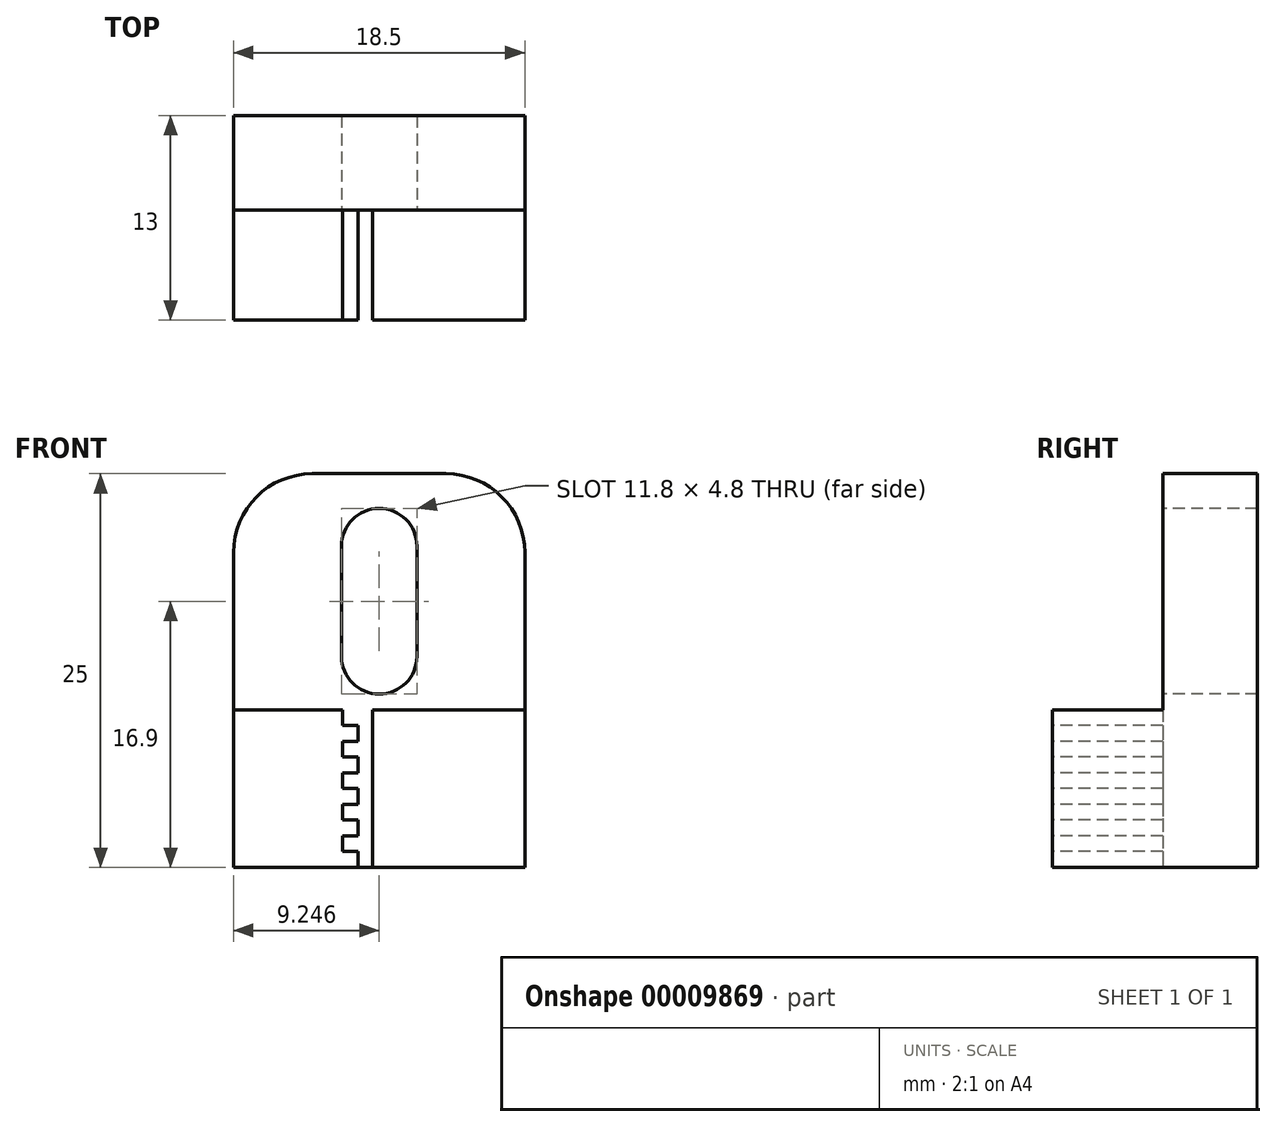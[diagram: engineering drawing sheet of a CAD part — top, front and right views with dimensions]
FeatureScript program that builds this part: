
annotation { "Feature Type Name" : "Feature", "Feature Type Description" : "" }
export const myFeature = defineFeature(function(context is Context, id is Id, definition is map)
    precondition{}
    {
        {
            var Q0;
            Q0=qCreatedBy(makeId("Top.planeOp"),FACE);
            var sketch = newSketch(context, id + "F0", { "sketchPlane" : qUnion([Q0])});
            skLineSegment(sketch, "E0.bottom", {"start": v(-4.96, 0) * mm, "end": v(13.54, 0) * mm});
            skLineSegment(sketch, "E0.top", {"start": v(-4.96, 25) * mm, "end": v(13.54, 25) * mm});
            skLineSegment(sketch, "E0.left", {"start": v(-4.96, 0) * mm, "end": v(-4.96, 25) * mm});
            skLineSegment(sketch, "E0.right", {"start": v(13.54, 0) * mm, "end": v(13.54, 25) * mm});
            skLineSegment(sketch, "E1", {"start": v(-4.96, 5) * mm, "end": v(13.54, 5) * mm});
            skLineSegment(sketch, "E2.bottom", {"start": v(-4.96, 17.95) * mm, "end": v(-1.96, 17.95) * mm});
            skLineSegment(sketch, "E2.top", {"start": v(-4.96, 12.05) * mm, "end": v(-1.96, 12.05) * mm});
            skLineSegment(sketch, "E2.left", {"start": v(-4.96, 17.95) * mm, "end": v(-4.96, 12.05) * mm});
            skLineSegment(sketch, "E2.right", {"start": v(-1.96, 17.95) * mm, "end": v(-1.96, 12.05) * mm});
            skLineSegment(sketch, "E3.bottom", {"start": v(13.54, 17.95) * mm, "end": v(10.54, 17.95) * mm});
            skLineSegment(sketch, "E3.top", {"start": v(13.54, 12.05) * mm, "end": v(10.54, 12.05) * mm});
            skLineSegment(sketch, "E3.left", {"start": v(13.54, 17.95) * mm, "end": v(13.54, 12.05) * mm});
            skLineSegment(sketch, "E3.right", {"start": v(10.54, 17.95) * mm, "end": v(10.54, 12.05) * mm});
            skPoint(sketch, "E4", {"position": v(-1.96, 15) * mm});
            skPoint(sketch, "E5", {"position": v(-4.96, 15) * mm});
            skLineSegment(sketch, "E6", {"start": v(-4.96, 15) * mm, "end": v(13.54, 15) * mm});
            skLineSegment(sketch, "E7", {"start": v(-4.96, 13) * mm, "end": v(13.54, 13) * mm});
            skSolve(sketch);
        }
        {
            var Q0;
            {var subQ0=sQuery(id+"F0.wireOp",EDGE,"E0.bottom");Q0=makeQuery(id+"F0.imprint","IMPRINT",FACE,{"disambiguationData":[TD([[makeQuery(id+"F0.imprint","IMPRINT",EDGE,{"derivedFrom":subQ0}),1.0]])]});}
            var Q1;
            {var subQ0=sQuery(id+"F0.wireOp",EDGE,"E1");Q1=makeQuery(id+"F0.imprint","IMPRINT",FACE,{"disambiguationData":[TD([[makeQuery(id+"F0.imprint","IMPRINT",EDGE,{"derivedFrom":subQ0}),1.0]])]});}
            var Q2;
            {var subQ0=sQuery(id+"F0.wireOp",EDGE,"E2.top");Q2=makeQuery(id+"F0.imprint","IMPRINT",FACE,{"disambiguationData":[TD([[makeQuery(id+"F0.imprint","IMPRINT",EDGE,{"derivedFrom":subQ0}),1.0]])]});}
            var Q3;
            {var subQ0=sQuery(id+"F0.wireOp",EDGE,"E3.top");Q3=makeQuery(id+"F0.imprint","IMPRINT",FACE,{"disambiguationData":[TD([[makeQuery(id+"F0.imprint","IMPRINT",EDGE,{"derivedFrom":subQ0}),-1.0]])]});}
            extrude(context, id + "F1", {"entities" : qUnion([Q0, Q1, Q2, Q3]), "depth" : 10 * mm});
        }
        {
            var Q0;
            Q0=makeQuery(id+"F1.opExtrude","SWEPT_FACE",FACE,{"disambiguationData":[OSD([sQuery(id+"F0.wireOp",EDGE,"E0.bottom")])]});
            var sketch = newSketch(context, id + "F2", { "sketchPlane" : qUnion([Q0])});
            skLineSegment(sketch, "E8", {"start": v(1.96, 10) * mm, "end": v(1.96, 9) * mm});
            skLineSegment(sketch, "E9", {"start": v(1.96, 9) * mm, "end": v(2.96, 9) * mm});
            skLineSegment(sketch, "E10", {"start": v(2.96, 9) * mm, "end": v(2.96, 8) * mm});
            skLineSegment(sketch, "E11", {"start": v(2.96, 8) * mm, "end": v(1.96, 8) * mm});
            skLineSegment(sketch, "E12", {"start": v(1.96, 8) * mm, "end": v(1.96, 7) * mm});
            skLineSegment(sketch, "E13", {"start": v(1.96, 7) * mm, "end": v(2.96, 7) * mm});
            skLineSegment(sketch, "E14", {"start": v(2.96, 7) * mm, "end": v(2.96, 6) * mm});
            skLineSegment(sketch, "E15", {"start": v(2.96, 6) * mm, "end": v(1.96, 6) * mm});
            skLineSegment(sketch, "E16", {"start": v(1.96, 6) * mm, "end": v(1.96, 5) * mm});
            skLineSegment(sketch, "E17", {"start": v(1.96, 5) * mm, "end": v(2.96, 5) * mm});
            skLineSegment(sketch, "E18", {"start": v(2.96, 5) * mm, "end": v(2.96, 4) * mm});
            skLineSegment(sketch, "E19", {"start": v(2.96, 4) * mm, "end": v(1.96, 4) * mm});
            skLineSegment(sketch, "E20", {"start": v(1.96, 4) * mm, "end": v(1.96, 3) * mm});
            skLineSegment(sketch, "E21", {"start": v(1.96, 3) * mm, "end": v(2.96, 3) * mm});
            skLineSegment(sketch, "E22", {"start": v(2.96, 3) * mm, "end": v(2.96, 2) * mm});
            skLineSegment(sketch, "E23", {"start": v(2.96, 2) * mm, "end": v(1.96, 2) * mm});
            skLineSegment(sketch, "E24", {"start": v(1.96, 2) * mm, "end": v(1.96, 1) * mm});
            skLineSegment(sketch, "E25", {"start": v(1.96, 1) * mm, "end": v(2.96, 1) * mm});
            skLineSegment(sketch, "E26", {"start": v(2.96, 1) * mm, "end": v(2.96, 0) * mm});
            skLineSegment(sketch, "E27", {"start": v(2.96, 0) * mm, "end": v(1.96, 0) * mm});
            skLineSegment(sketch, "E28", {"start": v(3.86, 10) * mm, "end": v(3.86, 0) * mm});
            skLineSegment(sketch, "E29", {"start": v(1.96, 10) * mm, "end": v(3.86, 10) * mm});
            skLineSegment(sketch, "E30", {"start": v(3.86, 0) * mm, "end": v(2.96, 0) * mm});
            skSolve(sketch);
        }
        {
            var Q0;
            Q0=makeQuery(id+"F2.imprint","IMPRINT",FACE,{"disambiguationData":[TD([[makeQuery(id+"F2.imprint","IMPRINT",EDGE,{"derivedFrom":sQuery(id+"F2.wireOp",EDGE,"E8")}),1.0]])]});
            extrude(context, id + "F3", {"entities" : qUnion([Q0]), "operationType" : NewBodyOperationType.REMOVE, "oppositeDirection" : true, "depth" : 7 * mm});
        }
        {
            var Q0;
            Q0=makeQuery(id+"F1.opExtrude","CAP_FACE",FACE,{"disambiguationData":[OSD([sQuery(id+"F0.wireOp",EDGE,"E0.bottom"),sQuery(id+"F0.wireOp",EDGE,"E0.left"),sQuery(id+"F0.wireOp",EDGE,"E0.right"),sQuery(id+"F0.wireOp",EDGE,"E7")])],"isStart":false});
            var sketch = newSketch(context, id + "F4", { "sketchPlane" : qUnion([Q0])});
            skLineSegment(sketch, "E31.bottom", {"start": v(-4.96, 0) * mm, "end": v(13.54, 0) * mm});
            skLineSegment(sketch, "E31.top", {"start": v(-4.96, 7) * mm, "end": v(13.54, 7) * mm});
            skLineSegment(sketch, "E31.left", {"start": v(-4.96, 7) * mm, "end": v(-4.96, 0) * mm});
            skLineSegment(sketch, "E31.right", {"start": v(13.54, 7) * mm, "end": v(13.54, 0) * mm});
            skSolve(sketch);
        }
        {
            var Q0;
            {var subQ0=makeQuery(id+"F1.opExtrude","CAP_EDGE",EDGE,{"disambiguationData":[OSD([sQuery(id+"F0.wireOp",EDGE,"E7")])],"isStart":false});Q0=makeQuery(id+"F4.imprint","IMPRINT",FACE,{"disambiguationData":[TD([[makeQuery(id+"F4.imprint","IMPRINT",EDGE,{"derivedFrom":subQ0}),-1.0]])]});}
            extrude(context, id + "F5", {"entities" : qUnion([Q0]), "operationType" : NewBodyOperationType.ADD, "depth" : 15 * mm});
        }
        {
            var Q0;
            Q0=makeQuery(id+"F5.boolean.opBoolean","MERGE",FACE,{"derivedFrom":[makeQuery(id+"F3.boolean.opBoolean","COPY",FACE,{"derivedFrom":makeQuery(id+"F3.opExtrude","CAP_FACE",FACE,{"disambiguationData":[OSD([sQuery(id+"F2.wireOp",EDGE,"E8"),sQuery(id+"F2.wireOp",EDGE,"E9"),sQuery(id+"F2.wireOp",EDGE,"E10"),sQuery(id+"F2.wireOp",EDGE,"E11"),sQuery(id+"F2.wireOp",EDGE,"E12"),sQuery(id+"F2.wireOp",EDGE,"E13"),sQuery(id+"F2.wireOp",EDGE,"E14"),sQuery(id+"F2.wireOp",EDGE,"E15"),sQuery(id+"F2.wireOp",EDGE,"E16"),sQuery(id+"F2.wireOp",EDGE,"E17"),sQuery(id+"F2.wireOp",EDGE,"E18"),sQuery(id+"F2.wireOp",EDGE,"E19"),sQuery(id+"F2.wireOp",EDGE,"E20"),sQuery(id+"F2.wireOp",EDGE,"E21"),sQuery(id+"F2.wireOp",EDGE,"E22"),sQuery(id+"F2.wireOp",EDGE,"E23"),sQuery(id+"F2.wireOp",EDGE,"E24"),sQuery(id+"F2.wireOp",EDGE,"E25"),sQuery(id+"F2.wireOp",EDGE,"E26"),sQuery(id+"F2.wireOp",EDGE,"E28"),sQuery(id+"F2.wireOp",EDGE,"E29"),sQuery(id+"F2.wireOp",EDGE,"E30")])],"isStart":false})}),makeQuery(id+"F5.opExtrude","SWEPT_FACE",FACE,{"disambiguationData":[OSD([sQuery(id+"F4.wireOp",EDGE,"E31.top")])]})]});
            var sketch = newSketch(context, id + "F6", { "sketchPlane" : qUnion([Q0])});
            skArc(sketch, "E32", {"start": v(6.69, 20.4) * mm, "mid": v(4.29, 22.8) * mm, "end": v(1.89, 20.4) * mm});
            skArc(sketch, "E33", {"start": v(1.89, 13.4) * mm, "mid": v(4.29, 11) * mm, "end": v(6.69, 13.4) * mm});
            skLineSegment(sketch, "E34", {"start": v(1.89, 20.4) * mm, "end": v(1.89, 13.4) * mm});
            skLineSegment(sketch, "E35", {"start": v(6.69, 20.4) * mm, "end": v(6.69, 13.4) * mm});
            skPoint(sketch, "E36", {"position": v(4.29, 25) * mm});
            skLineSegment(sketch, "E37", {"start": v(4.29, 10) * mm, "end": v(4.29, 11) * mm});
            skLineSegment(sketch, "E38", {"start": v(4.29, 22.8) * mm, "end": v(4.29, 25) * mm});
            skSolve(sketch);
        }
        {
            var Q0;
            Q0 = qSketchRegion(id + "F6", true);
            extrude(context, id + "F7", {"entities" : qUnion([Q0]), "operationType" : NewBodyOperationType.REMOVE, "oppositeDirection" : true, "depth" : 25 * mm});
        }
        {
            var Q0;
            Q0=makeQuery(id+"F5.opExtrude","CAP_EDGE",EDGE,{"disambiguationData":[OSD([sQuery(id+"F0.wireOp",EDGE,"E0.left"),sQuery(id+"F0.wireOp",EDGE,"E2.left")])],"isStart":false});
            var Q1;
            Q1=makeQuery(id+"F5.opExtrude","CAP_EDGE",EDGE,{"disambiguationData":[OSD([sQuery(id+"F0.wireOp",EDGE,"E0.right"),sQuery(id+"F0.wireOp",EDGE,"E3.left")])],"isStart":false});
            fillet(context, id + "F8", {"entities" : qUnion([Q0, Q1]), "radius" : 5 * mm, "tangentPropagation" : true, "allowEdgeOverflow" : false});
        }
    });
